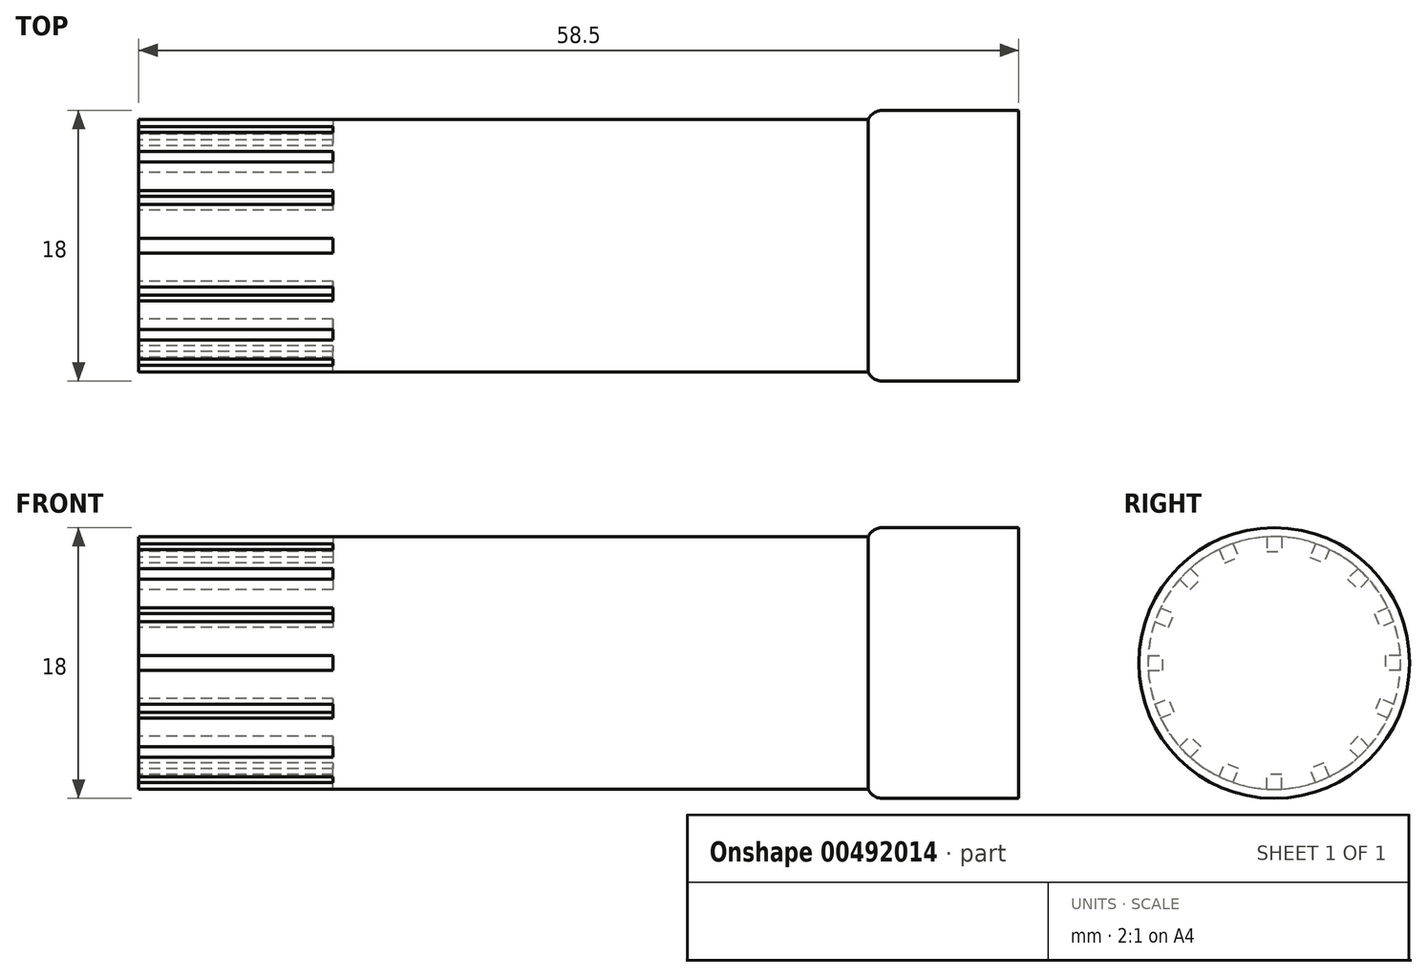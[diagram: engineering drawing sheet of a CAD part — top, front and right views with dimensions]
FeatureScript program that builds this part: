
annotation { "Feature Type Name" : "Feature", "Feature Type Description" : "" }
export const myFeature = defineFeature(function(context is Context, id is Id, definition is map)
    precondition{}
    {
        {
            var Q0;
            Q0=qCreatedBy(makeId("Right.planeOp"),FACE);
            var sketch = newSketch(context, id + "F0", { "sketchPlane" : qUnion([Q0])});
            skCircle(sketch, "E0", {"center": v(0, 0) * mm, "radius": 9 * mm});
            skSolve(sketch);
        }
        {
            var Q0;
            Q0 = qSketchRegion(id + "F0", true);
            extrude(context, id + "F1", {"entities" : qUnion([Q0]), "depth" : 10 * mm});
        }
        {
            var Q0;
            Q0=qCreatedBy(makeId("Right.planeOp"),FACE);
            var sketch = newSketch(context, id + "F2", { "sketchPlane" : qUnion([Q0])});
            skCircle(sketch, "E1", {"center": v(0, 0) * mm, "radius": 8.4 * mm});
            skSolve(sketch);
        }
        {
            var Q0;
            Q0=makeQuery(id+"F2.imprint","IMPRINT",FACE,{"disambiguationData":[TD([[makeQuery(id+"F2.imprint","IMPRINT",EDGE,{"derivedFrom":sQuery(id+"F2.wireOp",EDGE,"E1")}),1.0]])]});
            extrude(context, id + "F3", {"entities" : qUnion([Q0]), "operationType" : NewBodyOperationType.ADD, "oppositeDirection" : true, "depth" : 48.5 * mm});
        }
        {
            var Q0;
            Q0=makeQuery(id+"F1.opExtrude","CAP_EDGE",EDGE,{"disambiguationData":[OSD([sQuery(id+"F0.wireOp",EDGE,"E0")])],"isStart":true});
            fillet(context, id + "F4", {"entities" : qUnion([Q0]), "radius" : 1 * mm, "tangentPropagation" : true, "allowEdgeOverflow" : false});
        }
        {
            var Q0;
            Q0=makeQuery(id+"F3.opExtrude","CAP_FACE",FACE,{"disambiguationData":[OSD([sQuery(id+"F2.wireOp",EDGE,"E1")])],"isStart":false});
            var sketch = newSketch(context, id + "F5", { "sketchPlane" : qUnion([Q0])});
            skArc(sketch, "E2", {"start": v(0.5, 8.39) * mm, "mid": v(0, 8.4) * mm, "end": v(-0.5, 8.39) * mm});
            skLineSegment(sketch, "E3.top", {"start": v(0.5, 7.4) * mm, "end": v(-0.5, 7.4) * mm});
            skLineSegment(sketch, "E3.left", {"start": v(0.5, 8.39) * mm, "end": v(0.5, 7.4) * mm});
            skLineSegment(sketch, "E3.right", {"start": v(-0.5, 8.39) * mm, "end": v(-0.5, 7.4) * mm});
            skPoint(sketch, "E3.middle", {"position": v(0, 8.4) * mm});
            skPoint(sketch, "E4.1.0", {"position": v(-3.21, 7.76) * mm});
            skLineSegment(sketch, "E4.1.1", {"start": v(-2.75, 7.94) * mm, "end": v(-2.37, 7.03) * mm});
            skLineSegment(sketch, "E4.1.2", {"start": v(-2.37, 7.03) * mm, "end": v(-3.3, 6.65) * mm});
            skLineSegment(sketch, "E4.1.3", {"start": v(-3.67, 7.56) * mm, "end": v(-3.3, 6.65) * mm});
            skArc(sketch, "E4.1.4", {"start": v(-2.75, 7.94) * mm, "mid": v(-3.21, 7.76) * mm, "end": v(-3.67, 7.56) * mm});
            skPoint(sketch, "E4.2.0", {"position": v(-5.94, 5.94) * mm});
            skLineSegment(sketch, "E4.2.1", {"start": v(-5.58, 6.28) * mm, "end": v(-4.88, 5.59) * mm});
            skLineSegment(sketch, "E4.2.2", {"start": v(-4.88, 5.59) * mm, "end": v(-5.59, 4.88) * mm});
            skLineSegment(sketch, "E4.2.3", {"start": v(-6.28, 5.58) * mm, "end": v(-5.59, 4.88) * mm});
            skArc(sketch, "E4.2.4", {"start": v(-5.58, 6.28) * mm, "mid": v(-5.94, 5.94) * mm, "end": v(-6.28, 5.58) * mm});
            skLineSegment(sketch, "E5.1.3.0", {"start": v(-7.56, 3.67) * mm, "end": v(-6.65, 3.3) * mm});
            skLineSegment(sketch, "E5.4.3.0", {"start": v(-6.65, 3.3) * mm, "end": v(-7.03, 2.37) * mm});
            skPoint(sketch, "E5.6.3.0", {"position": v(-7.76, 3.21) * mm});
            skLineSegment(sketch, "E5.7.3.0", {"start": v(-7.94, 2.75) * mm, "end": v(-7.03, 2.37) * mm});
            skArc(sketch, "E5.10.3.0", {"start": v(-7.56, 3.67) * mm, "mid": v(-7.76, 3.21) * mm, "end": v(-7.94, 2.75) * mm});
            skLineSegment(sketch, "E5.1.4.0", {"start": v(-8.39, 0.5) * mm, "end": v(-7.4, 0.5) * mm});
            skLineSegment(sketch, "E5.4.4.0", {"start": v(-7.4, 0.5) * mm, "end": v(-7.4, -0.5) * mm});
            skPoint(sketch, "E5.6.4.0", {"position": v(-8.4, 0) * mm});
            skLineSegment(sketch, "E5.7.4.0", {"start": v(-8.39, -0.5) * mm, "end": v(-7.4, -0.5) * mm});
            skArc(sketch, "E5.10.4.0", {"start": v(-8.39, 0.5) * mm, "mid": v(-8.4, 0) * mm, "end": v(-8.39, -0.5) * mm});
            skLineSegment(sketch, "E5.1.5.0", {"start": v(-7.94, -2.75) * mm, "end": v(-7.03, -2.37) * mm});
            skLineSegment(sketch, "E5.4.5.0", {"start": v(-7.03, -2.37) * mm, "end": v(-6.65, -3.3) * mm});
            skPoint(sketch, "E5.6.5.0", {"position": v(-7.76, -3.21) * mm});
            skLineSegment(sketch, "E5.7.5.0", {"start": v(-7.56, -3.67) * mm, "end": v(-6.65, -3.3) * mm});
            skArc(sketch, "E5.10.5.0", {"start": v(-7.94, -2.75) * mm, "mid": v(-7.76, -3.21) * mm, "end": v(-7.56, -3.67) * mm});
            skLineSegment(sketch, "E5.1.6.0", {"start": v(-6.28, -5.58) * mm, "end": v(-5.59, -4.88) * mm});
            skLineSegment(sketch, "E5.4.6.0", {"start": v(-5.59, -4.88) * mm, "end": v(-4.88, -5.59) * mm});
            skPoint(sketch, "E5.6.6.0", {"position": v(-5.94, -5.94) * mm});
            skLineSegment(sketch, "E5.7.6.0", {"start": v(-5.58, -6.28) * mm, "end": v(-4.88, -5.59) * mm});
            skArc(sketch, "E5.10.6.0", {"start": v(-6.28, -5.58) * mm, "mid": v(-5.94, -5.94) * mm, "end": v(-5.58, -6.28) * mm});
            skLineSegment(sketch, "E5.1.7.0", {"start": v(-3.67, -7.56) * mm, "end": v(-3.3, -6.65) * mm});
            skLineSegment(sketch, "E5.4.7.0", {"start": v(-3.3, -6.65) * mm, "end": v(-2.37, -7.03) * mm});
            skPoint(sketch, "E5.6.7.0", {"position": v(-3.21, -7.76) * mm});
            skLineSegment(sketch, "E5.7.7.0", {"start": v(-2.75, -7.94) * mm, "end": v(-2.37, -7.03) * mm});
            skArc(sketch, "E5.10.7.0", {"start": v(-3.67, -7.56) * mm, "mid": v(-3.21, -7.76) * mm, "end": v(-2.75, -7.94) * mm});
            skLineSegment(sketch, "E5.1.8.0", {"start": v(-0.5, -8.39) * mm, "end": v(-0.5, -7.4) * mm});
            skLineSegment(sketch, "E5.4.8.0", {"start": v(-0.5, -7.4) * mm, "end": v(0.5, -7.4) * mm});
            skPoint(sketch, "E5.6.8.0", {"position": v(0, -8.4) * mm});
            skLineSegment(sketch, "E5.7.8.0", {"start": v(0.5, -8.39) * mm, "end": v(0.5, -7.4) * mm});
            skArc(sketch, "E5.10.8.0", {"start": v(-0.5, -8.39) * mm, "mid": v(0, -8.4) * mm, "end": v(0.5, -8.39) * mm});
            skLineSegment(sketch, "E5.1.9.0", {"start": v(2.75, -7.94) * mm, "end": v(2.37, -7.03) * mm});
            skLineSegment(sketch, "E5.4.9.0", {"start": v(2.37, -7.03) * mm, "end": v(3.3, -6.65) * mm});
            skPoint(sketch, "E5.6.9.0", {"position": v(3.21, -7.76) * mm});
            skLineSegment(sketch, "E5.7.9.0", {"start": v(3.67, -7.56) * mm, "end": v(3.3, -6.65) * mm});
            skArc(sketch, "E5.10.9.0", {"start": v(2.75, -7.94) * mm, "mid": v(3.21, -7.76) * mm, "end": v(3.67, -7.56) * mm});
            skLineSegment(sketch, "E5.1.10.0", {"start": v(5.58, -6.28) * mm, "end": v(4.88, -5.59) * mm});
            skLineSegment(sketch, "E5.4.10.0", {"start": v(4.88, -5.59) * mm, "end": v(5.59, -4.88) * mm});
            skPoint(sketch, "E5.6.10.0", {"position": v(5.94, -5.94) * mm});
            skLineSegment(sketch, "E5.7.10.0", {"start": v(6.28, -5.58) * mm, "end": v(5.59, -4.88) * mm});
            skArc(sketch, "E5.10.10.0", {"start": v(5.58, -6.28) * mm, "mid": v(5.94, -5.94) * mm, "end": v(6.28, -5.58) * mm});
            skLineSegment(sketch, "E5.1.11.0", {"start": v(7.56, -3.67) * mm, "end": v(6.65, -3.3) * mm});
            skLineSegment(sketch, "E5.4.11.0", {"start": v(6.65, -3.3) * mm, "end": v(7.03, -2.37) * mm});
            skPoint(sketch, "E5.6.11.0", {"position": v(7.76, -3.21) * mm});
            skLineSegment(sketch, "E5.7.11.0", {"start": v(7.94, -2.75) * mm, "end": v(7.03, -2.37) * mm});
            skArc(sketch, "E5.10.11.0", {"start": v(7.56, -3.67) * mm, "mid": v(7.76, -3.21) * mm, "end": v(7.94, -2.75) * mm});
            skLineSegment(sketch, "E5.1.12.0", {"start": v(8.39, -0.5) * mm, "end": v(7.4, -0.5) * mm});
            skLineSegment(sketch, "E5.4.12.0", {"start": v(7.4, -0.5) * mm, "end": v(7.4, 0.5) * mm});
            skPoint(sketch, "E5.6.12.0", {"position": v(8.4, 0) * mm});
            skLineSegment(sketch, "E5.7.12.0", {"start": v(8.39, 0.5) * mm, "end": v(7.4, 0.5) * mm});
            skArc(sketch, "E5.10.12.0", {"start": v(8.39, -0.5) * mm, "mid": v(8.4, 0) * mm, "end": v(8.39, 0.5) * mm});
            skLineSegment(sketch, "E5.1.13.0", {"start": v(7.94, 2.75) * mm, "end": v(7.03, 2.37) * mm});
            skLineSegment(sketch, "E5.4.13.0", {"start": v(7.03, 2.37) * mm, "end": v(6.65, 3.3) * mm});
            skPoint(sketch, "E5.6.13.0", {"position": v(7.76, 3.21) * mm});
            skLineSegment(sketch, "E5.7.13.0", {"start": v(7.56, 3.67) * mm, "end": v(6.65, 3.3) * mm});
            skArc(sketch, "E5.10.13.0", {"start": v(7.94, 2.75) * mm, "mid": v(7.76, 3.21) * mm, "end": v(7.56, 3.67) * mm});
            skLineSegment(sketch, "E5.1.14.0", {"start": v(6.28, 5.58) * mm, "end": v(5.59, 4.88) * mm});
            skLineSegment(sketch, "E5.4.14.0", {"start": v(5.59, 4.88) * mm, "end": v(4.88, 5.59) * mm});
            skPoint(sketch, "E5.6.14.0", {"position": v(5.94, 5.94) * mm});
            skLineSegment(sketch, "E5.7.14.0", {"start": v(5.58, 6.28) * mm, "end": v(4.88, 5.59) * mm});
            skArc(sketch, "E5.10.14.0", {"start": v(6.28, 5.58) * mm, "mid": v(5.94, 5.94) * mm, "end": v(5.58, 6.28) * mm});
            skLineSegment(sketch, "E5.1.15.0", {"start": v(3.67, 7.56) * mm, "end": v(3.3, 6.65) * mm});
            skLineSegment(sketch, "E5.4.15.0", {"start": v(3.3, 6.65) * mm, "end": v(2.37, 7.03) * mm});
            skPoint(sketch, "E5.6.15.0", {"position": v(3.21, 7.76) * mm});
            skLineSegment(sketch, "E5.7.15.0", {"start": v(2.75, 7.94) * mm, "end": v(2.37, 7.03) * mm});
            skArc(sketch, "E5.10.15.0", {"start": v(3.67, 7.56) * mm, "mid": v(3.21, 7.76) * mm, "end": v(2.75, 7.94) * mm});
            skSolve(sketch);
        }
        {
            var Q0;
            Q0 = qSketchRegion(id + "F5", true);
            extrude(context, id + "F6", {"entities" : qUnion([Q0]), "operationType" : NewBodyOperationType.REMOVE, "oppositeDirection" : true, "depth" : 12.92 * mm});
        }
    });
